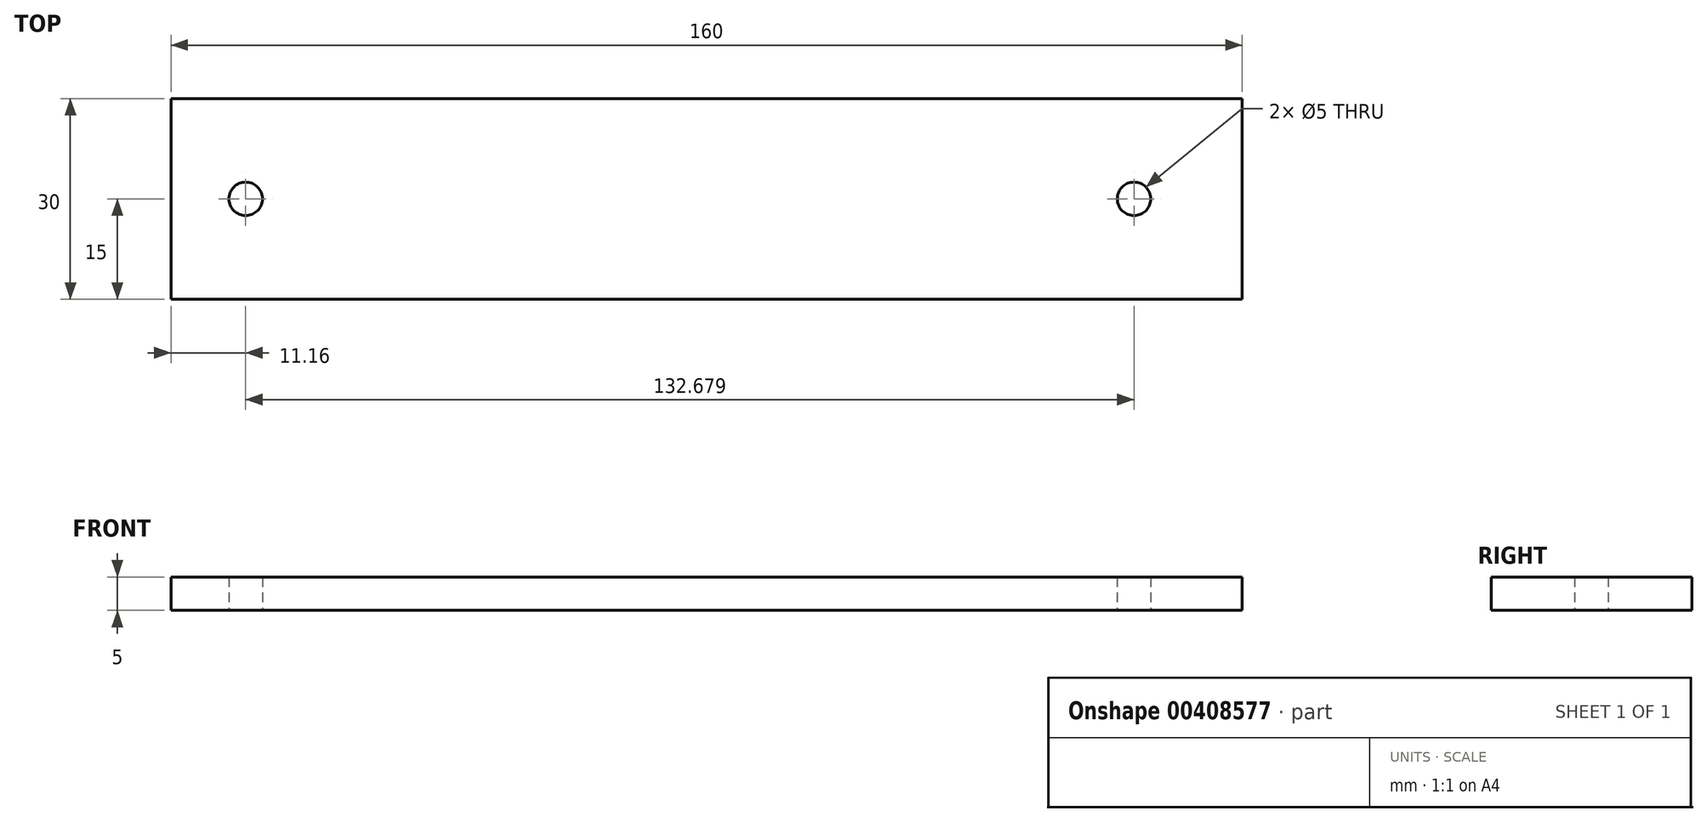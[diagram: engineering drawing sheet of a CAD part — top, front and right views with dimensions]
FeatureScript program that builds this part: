
annotation { "Feature Type Name" : "Feature", "Feature Type Description" : "" }
export const myFeature = defineFeature(function(context is Context, id is Id, definition is map)
    precondition{}
    {
        {
            var Q0;
            Q0=qCreatedBy(makeId("Top.planeOp"),FACE);
            var sketch = newSketch(context, id + "F0", { "sketchPlane" : qUnion([Q0])});
            skCircle(sketch, "E0", {"center": v(63.84, 0) * mm, "radius": 2.5 * mm});
            skCircle(sketch, "E1", {"center": v(-68.84, 0) * mm, "radius": 2.5 * mm});
            skLineSegment(sketch, "E2.bottom", {"start": v(-80, 15) * mm, "end": v(80, 15) * mm});
            skLineSegment(sketch, "E2.top", {"start": v(-80, -15) * mm, "end": v(80, -15) * mm});
            skLineSegment(sketch, "E2.left", {"start": v(-80, 15) * mm, "end": v(-80, -15) * mm});
            skLineSegment(sketch, "E2.right", {"start": v(80, 15) * mm, "end": v(80, -15) * mm});
            skSolve(sketch);
        }
        {
            var Q0;
            Q0=makeQuery(id+"F0.imprint","IMPRINT",FACE,{"disambiguationData":[TD([[makeQuery(id+"F0.imprint","IMPRINT",EDGE,{"derivedFrom":sQuery(id+"F0.wireOp",EDGE,"E0")}),-1.0]])]});
            extrude(context, id + "F1", {"entities" : qUnion([Q0]), "depth" : 5 * mm, "offsetDistance" : 25 * mm});
        }
    });
